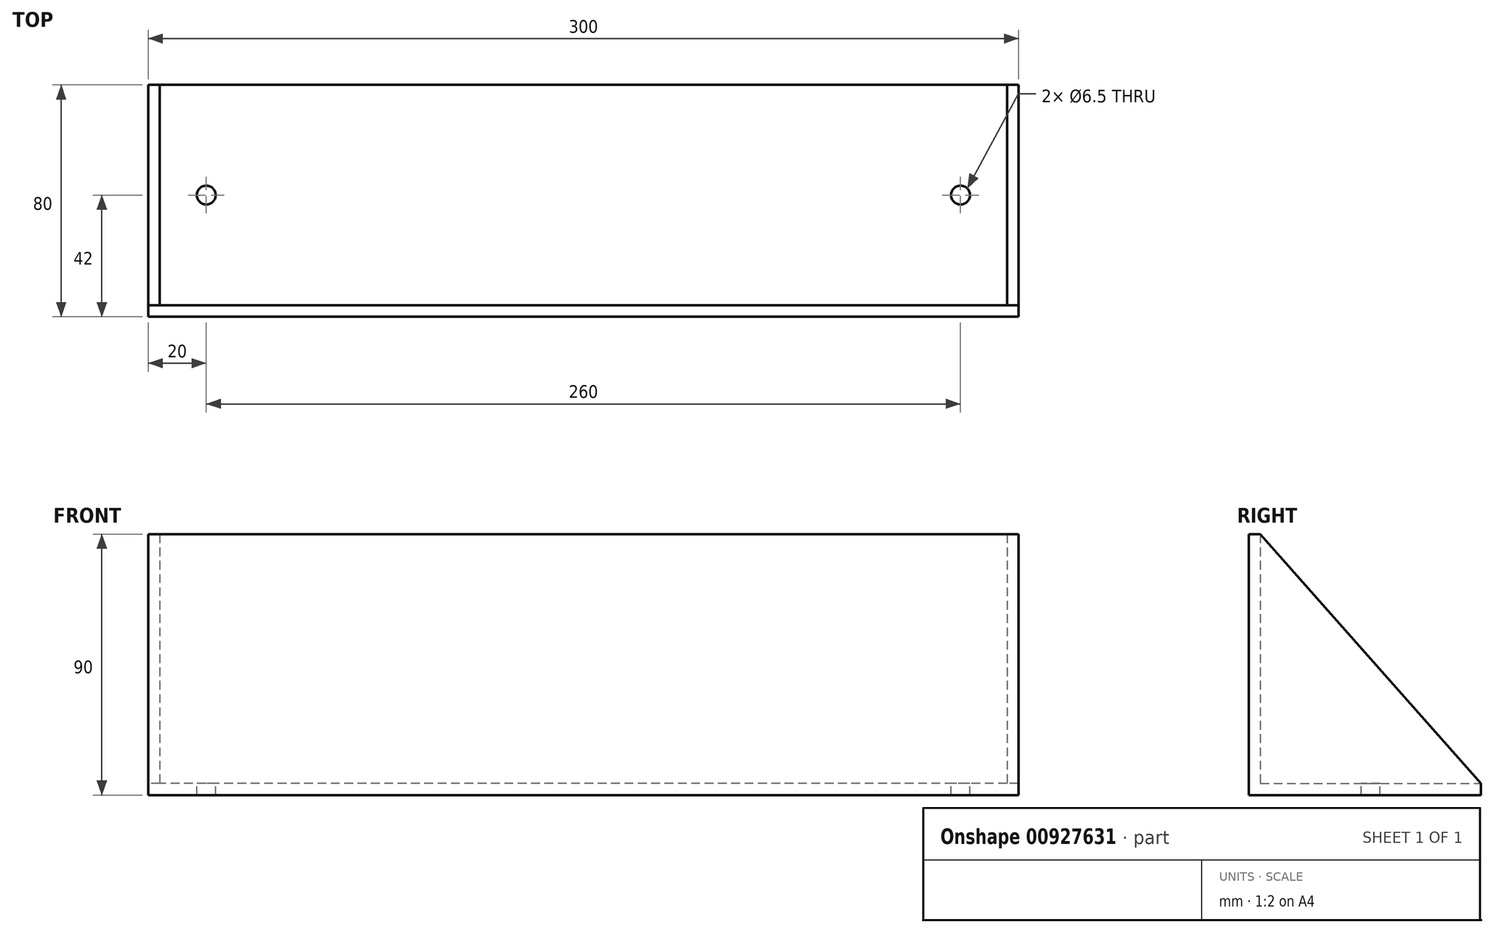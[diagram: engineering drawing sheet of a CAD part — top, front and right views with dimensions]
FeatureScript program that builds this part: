
annotation { "Feature Type Name" : "Feature", "Feature Type Description" : "" }
export const myFeature = defineFeature(function(context is Context, id is Id, definition is map)
    precondition{}
    {
        {
            var Q0;
            Q0=qCreatedBy(makeId("Right.planeOp"),FACE);
            var sketch = newSketch(context, id + "F0", { "sketchPlane" : qUnion([Q0])});
            skLineSegment(sketch, "E0", {"start": v(0, 0) * mm, "end": v(80, 0) * mm});
            skLineSegment(sketch, "E1", {"start": v(0, 0) * mm, "end": v(0, 90) * mm});
            skLineSegment(sketch, "E2.0", {"start": v(4, 4) * mm, "end": v(4, 90) * mm});
            skLineSegment(sketch, "E2.1", {"start": v(4, 4) * mm, "end": v(80, 4) * mm});
            skLineSegment(sketch, "E3", {"start": v(0, 90) * mm, "end": v(4, 90) * mm});
            skLineSegment(sketch, "E4", {"start": v(80, 4) * mm, "end": v(80, 0) * mm});
            skSolve(sketch);
        }
        {
            var Q0;
            Q0 = qSketchRegion(id + "F0", true);
            extrude(context, id + "F1", {"entities" : qUnion([Q0]), "depth" : 300 * mm, "offsetDistance" : 25 * mm});
        }
        {
            var Q0;
            Q0=makeQuery(id+"F1.opExtrude","SWEPT_FACE",FACE,{"disambiguationData":[OSD([sQuery(id+"F0.wireOp",EDGE,"E2.1")])]});
            var sketch = newSketch(context, id + "F2", { "sketchPlane" : qUnion([Q0])});
            skPoint(sketch, "E5.startSnap0", {"position": v(150, 80) * mm});
            skLineSegment(sketch, "E6", {"start": v(-15.94, 42) * mm, "end": v(63.1, 42) * mm, "construction": true});
            skPoint(sketch, "E6.startSnap0", {"position": v(0, 42) * mm});
            skPoint(sketch, "E7", {"position": v(20, 42) * mm});
            skCircle(sketch, "E8", {"center": v(20, 42) * mm, "radius": 3.25 * mm});
            skLineSegment(sketch, "E9", {"start": v(150, 72.2) * mm, "end": v(150, -45.46) * mm, "construction": true});
            skPoint(sketch, "E10.MirrorP", {"position": v(280, 42) * mm});
            skCircle(sketch, "E11.MirrorC", {"center": v(280, 42) * mm, "radius": 3.25 * mm});
            skSolve(sketch);
        }
        {
            var Q0;
            Q0 = qSketchRegion(id + "F2", true);
            extrude(context, id + "F3", {"entities" : qUnion([Q0]), "operationType" : NewBodyOperationType.REMOVE, "oppositeDirection" : true, "depth" : 25 * mm, "offsetDistance" : 25 * mm});
        }
        {
            var Q0;
            Q0=qCreatedBy(makeId("Right.planeOp"),FACE);
            var sketch = newSketch(context, id + "F4", { "sketchPlane" : qUnion([Q0])});
            skLineSegment(sketch, "E12", {"start": v(80, 4) * mm, "end": v(4, 90) * mm});
            skLineSegment(sketch, "E13", {"start": v(4, 90) * mm, "end": v(4, 4) * mm});
            skLineSegment(sketch, "E14", {"start": v(4, 4) * mm, "end": v(80, 4) * mm});
            skSolve(sketch);
        }
        {
            var Q0;
            Q0 = qSketchRegion(id + "F4", true);
            extrude(context, id + "F5", {"entities" : qUnion([Q0]), "operationType" : NewBodyOperationType.ADD, "depth" : 4 * mm, "offsetDistance" : 25 * mm});
        }
        {
            var Q0;
            Q0=qCreatedBy(makeId("Right.planeOp"),FACE);
            cPlane(context, id + "F6", {"entities" : qUnion([Q0]), "cplaneType" : CPlaneType.OFFSET, "offset" : 300 * mm, "width" : 150 * mm, "height" : 150 * mm});
        }
        {
            var Q0;
            Q0=qCreatedBy(id+"F6.planeOp",FACE);
            var sketch = newSketch(context, id + "F7", { "sketchPlane" : qUnion([Q0])});
            skLineSegment(sketch, "E15", {"start": v(4, 90) * mm, "end": v(4, 4) * mm});
            skLineSegment(sketch, "E16", {"start": v(4, 4) * mm, "end": v(80, 4) * mm});
            skLineSegment(sketch, "E17", {"start": v(80, 4) * mm, "end": v(4, 90) * mm});
            skSolve(sketch);
        }
        {
            var Q0;
            Q0 = qSketchRegion(id + "F7", true);
            extrude(context, id + "F8", {"entities" : qUnion([Q0]), "operationType" : NewBodyOperationType.ADD, "oppositeDirection" : true, "depth" : 4 * mm, "offsetDistance" : 25 * mm});
        }
    });
